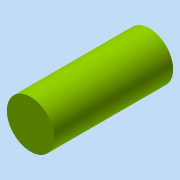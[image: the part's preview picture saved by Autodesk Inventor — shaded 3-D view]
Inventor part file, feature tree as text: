
AUTODESK INVENTOR PART (.ipt)
format: ipt  version: 2015 (Build 190159000, 159)  size: 81,408 bytes
history: native  units: in
note: dims shown in document units (in); Inventor stores cm internally (conversion verified against a paired STEP export)
features: extrude x1, sketch x1
ambient origin geometry x8: Origin, YZ Plane, XZ Plane, XY Plane, X Axis, Y Axis, Z Axis, Center Point
bodies: Solid1 (feature_tree)
feature tree (2):
  extrude  "Extrusion1"  Depth=2.5591in TaperAngle=0.0deg
  sketch  "Sketch1"  dims[d0=1.0236in d1=2.5591in d2=0.0in]
